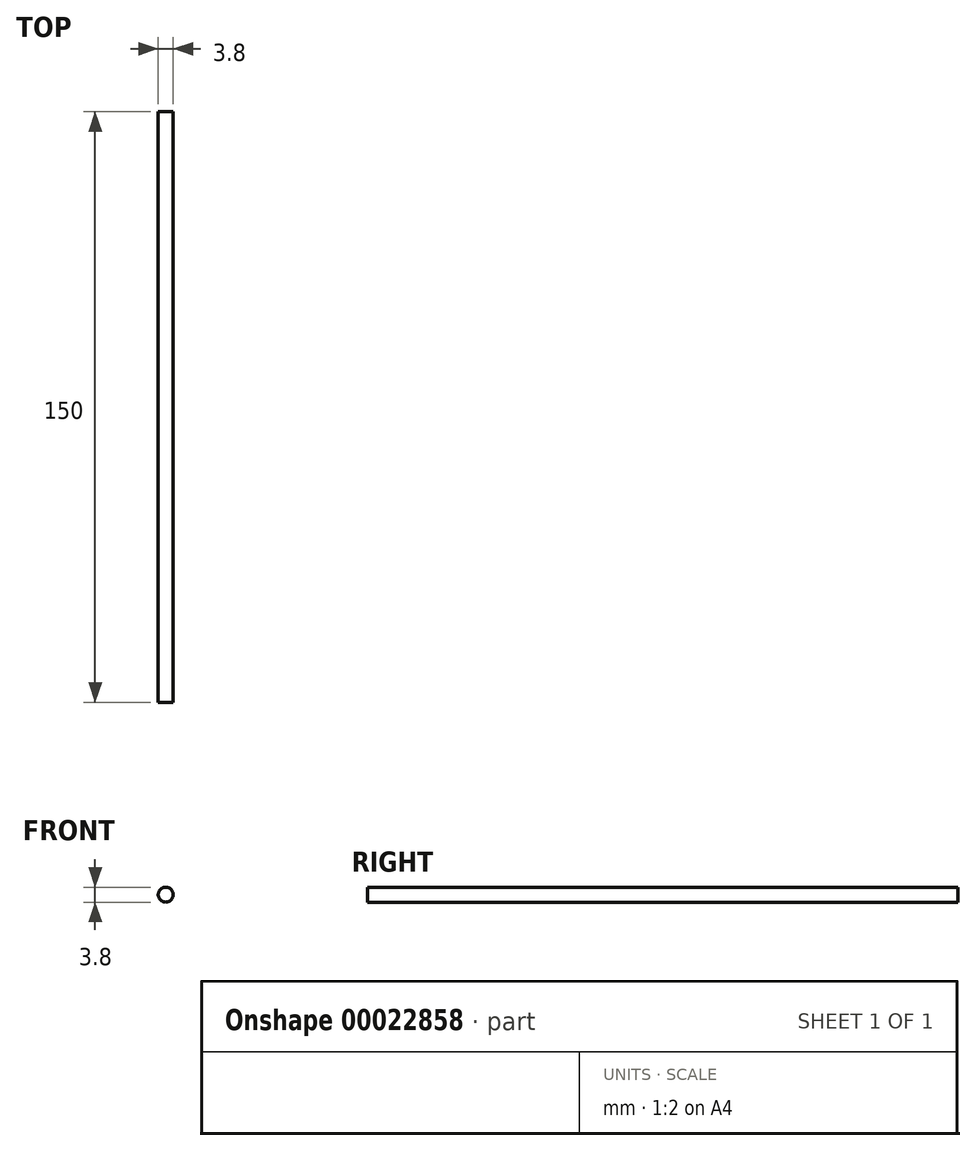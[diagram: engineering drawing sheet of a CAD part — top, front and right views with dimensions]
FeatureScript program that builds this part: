
annotation { "Feature Type Name" : "Feature", "Feature Type Description" : "" }
export const myFeature = defineFeature(function(context is Context, id is Id, definition is map)
    precondition{}
    {
        {
            var Q0;
            Q0=qCreatedBy(makeId("Top.planeOp"),FACE);
            var sketch = newSketch(context, id + "F0", { "sketchPlane" : qUnion([Q0])});
            skLineSegment(sketch, "E0", {"start": v(42.16, 141.07) * mm, "end": v(42.16, -8.93) * mm});
            skLineSegment(sketch, "E1", {"start": v(44.06, 141.07) * mm, "end": v(44.06, 19.15) * mm});
            skLineSegment(sketch, "E2", {"start": v(44.06, 19.15) * mm, "end": v(44.06, -8.93) * mm});
            skLineSegment(sketch, "E3", {"start": v(42.16, 141.07) * mm, "end": v(44.06, 141.07) * mm});
            skLineSegment(sketch, "E4", {"start": v(42.16, 19.15) * mm, "end": v(44.06, 19.15) * mm});
            skLineSegment(sketch, "E5", {"start": v(42.16, -8.93) * mm, "end": v(44.06, -8.93) * mm});
            skSolve(sketch);
        }
        {
            var Q0;
            Q0=qSketchRegion(id+"F0",true);
            var Q1;
            Q1=sQuery(id+"F0.wireOp",EDGE,"E0");
            revolve(context, id + "F1", {"entities" : qUnion([Q0]), "axis" : qUnion([Q1]), "revolveType" : RevolveType.FULL});
        }
    });
